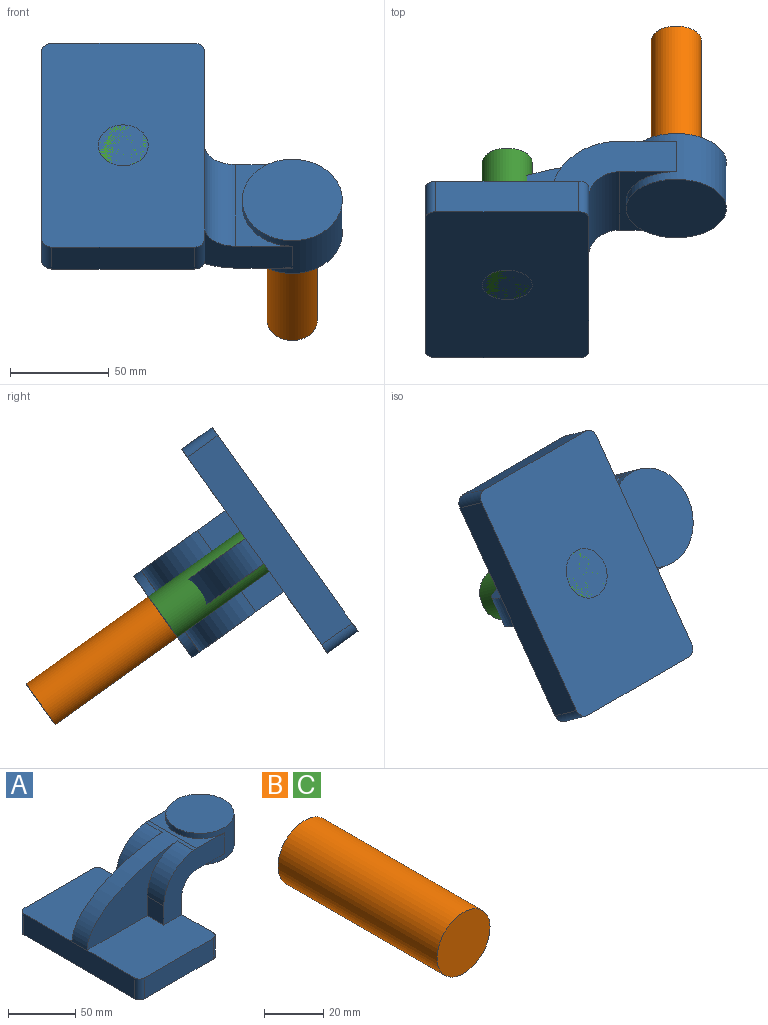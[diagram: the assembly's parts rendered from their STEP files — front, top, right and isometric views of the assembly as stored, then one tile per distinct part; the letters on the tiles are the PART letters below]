
ASSEMBLY  parts=3 mates=2
PART A: 26 faces, bbox 152.4x127x76.2 mm
  f0: plane 17.48x17.46mm, normal (-1,0,0), area 305.2mm2, adj f1,f2,f16,f18
  f1: plane 82.55x55.56mm, normal (0,0,1), area 4242.9mm2, adj f0,f4,f6,f8,f16,f18,f22,f23
  f2: cylinder r=34.92mm len=34.77mm, axis (0,1,0), area 900.9mm2, adj f0,f9,f16,f18
  f3: plane 82.55x55.56mm, normal (0,0,1), area 4242.9mm2, adj f4,f6,f7,f11,f15,f17,f24,f25
  f4: plane 116.84x19.05mm, normal (-1,0,0), area 2225.8mm2, adj f1,f3,f5,f9,f23,f25
  f5: plane 127x82.55mm, normal (0,0,-1), area 10461.7mm2, adj f4,f6,f7,f8,f22,f23,f24,f25
  f6: plane 116.84x36.53mm, normal (1,0,0), area 3113.5mm2, adj f1,f3,f5,f12,f15,f16,f22,f24
  f7: plane 72.39x19.05mm, normal (0,-1,0), area 1379mm2, adj f3,f5,f24,f25
  f8: plane 72.39x19.05mm, normal (0,1,0), area 1379mm2, adj f1,f5,f22,f23
  f9: extruded ~98.43x52.4mm, area 2006.6mm2, adj f2,f4,f10,f14,f15,f16,f17,f18
  f10: cylinder r=34.92mm len=34.77mm, axis (0,1,0), area 900.9mm2, adj f9,f11,f15,f17
  f11: plane 17.48x17.46mm, normal (-1,0,0), area 305.2mm2, adj f3,f10,f15,f17
  f12: cylinder r=15.88mm len=50.8mm, axis (0,1,0), area 1266.8mm2, adj f6,f13,f15,f16
  f13: plane 50.8x28.58mm, normal (0,0,-1), area 438.2mm2, adj f12,f15,f16,f19
  f14: plane 50.8x28.58mm, normal (0,0,1), area 438.2mm2, adj f9,f15,f16,f19
  f15: plane 63.5x52.4mm, normal (0,-1,0), area 1637.3mm2, adj f3,f6,f9,f10,f11,f12,f13,f14
  f16: plane 63.5x52.4mm, normal (0,1,0), area 1637.3mm2, adj f0,f1,f2,f6,f9,f12,f13,f14
  f17: plane 98.43x52.4mm, normal (0,-1,0), area 2298.4mm2, adj f3,f9,f10,f11
  f18: plane 98.43x52.4mm, normal (0,1,0), area 2298.4mm2, adj f0,f1,f2,f9
  f19: cylinder r=25.4mm len=50.8mm, axis (0,0,-1), area 3040.2mm2, adj f13,f14,f15,f16,f20,f21
  f20: plane 50.8x50.8mm, normal (0,0,-1), area 2026.8mm2, adj f19
  f21: plane 50.8x50.8mm, normal (0,0,1), area 2026.8mm2, adj f19
  f22: cylinder r=5.08mm len=19.05mm, axis (0,0,1), area 152mm2, adj f1,f5,f6,f8
  f23: cylinder r=5.08mm len=19.05mm, axis (0,0,-1), area 152mm2, adj f1,f4,f5,f8
  f24: cylinder r=5.08mm len=19.05mm, axis (0,0,-1), area 152mm2, adj f3,f5,f6,f7
  f25: cylinder r=5.08mm len=19.05mm, axis (0,0,1), area 152mm2, adj f3,f4,f5,f7
PART B: 3 faces, bbox 25.4x76.2x25.4 mm
  f0: cylinder r=12.7mm len=76.2mm, axis (0,1,0), area 6080.5mm2, adj f1,f2
  f1: plane 25.4x25.4mm, normal (0,-1,0), area 506.7mm2, adj f0
  f2: plane 25.4x25.4mm, normal (0,1,0), area 506.7mm2, adj f0
PART C: same geometry as B
PLACE A rot(axis=(-1,0,0),125.6deg) t=(34.32,-63.51,178.68)mm
PLACE B rot(axis=(-1,0,0),35.6deg) t=(195.86,75.41,18.18)mm
PLACE C rot(axis=(-1,0,0),35.6deg) t=(110.13,13.44,62.52)mm
MATE fastened C.f0 <-> A.f5  axis (0,-0.81,0.58) through (34.32,-71.26,184.22)mm
MATE fastened B.f0 <-> A.f19  axis (0,0.81,-0.58) through (120.05,-9.29,139.89)mm
